# Revit family: 05-60-001-DN50-300.rfatest
name_source: partatom
category: Pipe Accessories
units: mm (PartAtom-declared; Revit-internal decimal feet)

## family parameters
Always vertical = Yes
Cut with Voids When Loaded = No
Part Type = Valve - Breaks Into
Round Connector Dimension = Use Diameter
Shared = No
Work Plane-Based = No

## types (18) — shared parameters
1 = 1 mm  [stored 0.00328084 ft]
10 = 10 mm  [stored 0.0328084 ft]
3 = 3 mm  [stored 0.00984252 ft]
5 = 5 mm  [stored 0.0164042 ft]
DN050_ PN10/16_Dd63 = 05-050-60-1600
DN060_ PN10/16_Dd63 = 05-063-60-1600
DN065_ PN10/16_Dd75 = 05-075-60-1600
DN080_ PN10/16_Dd90 = 05-090-60-1600
DN100_ PN10/16_Dd110 = 05-110-60-1600
DN125_ PN10/16_Dd125 = 05-125-60-1600
DN125_ PN10/16_Dd140 = 05-140-60-1600
DN150_ PN10/16_Dd160 = 05-160-60-1600
DN200_ PN10_Dd200 = 05-200-60-0600
DN200_ PN10_Dd225 = 05-200-60-1600
DN200_ PN16_Dd200 = 05-225-60-0600
DN200_ PN16_Dd225 = 05-225-60-1600
DN250_ PN10_Dd250 = 05-250-60-0600
DN250_ PN10_Dd280 = 05-250-60-1600
DN250_ PN16_Dd250 = 05-280-60-0600
DN250_ PN16_Dd280 = 05-280-60-1600
DN300_ PN10_Dd315 = 05-315-60-0600
DN300_ PN16_Dd315 = 05-315-60-1600
Description_ = AVK COMBI-FLANGE FOR PE AND PVC PIPES, PN10/16
EPDM = 6 mm  [stored 0.019685 ft]
Epdm = 2 mm  [stored 0.00656168 ft]
FL_T1 = 3 mm  [stored 0.00984252 ft]
Search_table = 05-60-001-DN50-300
URL_product_pages = https://www.avkvalves.com
zero-valued in all types: Default Elevation, L4

## per-type parameters (varying)
| type | (D-Dd)1 | Bore | D | DN | Dd | FL_T | Flange_H | L | L-L9 | L/2 | L1 | L2 | L6 | L9 | Thickness | Thickness1 |
| DN100_ PN10/16_Dd110 | 19 mm  [stored 0.062336 ft] | 50 mm  [stored 0.164042 ft] | 110 mm | 100 mm | 55 mm  [stored 0.180446 ft] | 5 mm  [stored 0.0164042 ft] | 8 mm  [stored 0.0262467 ft] | 99 mm | 72 mm | 50 mm  [stored 0.164042 ft] | 35 mm | 149 mm | 20 mm  [stored 0.0656168 ft] | 27 mm  [stored 0.0885827 ft] | 5 mm  [stored 0.0164042 ft] | 10 mm  [stored 0.0328084 ft] |
| DN125_ PN10/16_Dd125 | 22 mm | 63 mm  [stored 0.206693 ft] | 125 mm | 125 mm | 63 mm  [stored 0.206693 ft] | 5 mm  [stored 0.0164042 ft] | 9 mm  [stored 0.0295276 ft] | 101 mm | 74 mm | 51 mm | 35 mm | 152 mm | 20 mm  [stored 0.0656168 ft] | 27 mm  [stored 0.0885827 ft] | 5 mm  [stored 0.0164042 ft] | 10 mm  [stored 0.0328084 ft] |
| DN125_ PN10/16_Dd140 | 19 mm  [stored 0.062336 ft] | 63 mm  [stored 0.206693 ft] | 125 mm | 125 mm | 70 mm | 5 mm  [stored 0.0164042 ft] | 8 mm  [stored 0.0262467 ft] | 103 mm | 76 mm | 52 mm | 35 mm | 155 mm | 21 mm  [stored 0.0688976 ft] | 27 mm  [stored 0.0885827 ft] | 5 mm  [stored 0.0164042 ft] | 10 mm  [stored 0.0328084 ft] |
| DN150_ PN10/16_Dd160 | 22 mm | 75 mm | 143 mm | 150 mm | 80 mm | 5 mm  [stored 0.0164042 ft] | 9 mm  [stored 0.0295276 ft] | 105 mm | 78 mm | 53 mm | 35 mm | 158 mm | 21 mm  [stored 0.0688976 ft] | 27 mm  [stored 0.0885827 ft] | 5 mm  [stored 0.0164042 ft] | 10 mm  [stored 0.0328084 ft] |
| DN200_ PN10_Dd200 | 25 mm  [stored 0.082021 ft] | 100 mm | 170 mm | 200 mm | 100 mm | 8 mm  [stored 0.0262467 ft] | 11 mm | 107 mm | 80 mm | 54 mm | 35 mm | 161 mm | 21 mm  [stored 0.0688976 ft] | 27 mm  [stored 0.0885827 ft] | 6 mm  [stored 0.019685 ft] | 15 mm  [stored 0.0492126 ft] |
| DN200_ PN10_Dd225 | 20 mm  [stored 0.0656168 ft] | 100 mm | 170 mm | 200 mm | 113 mm | 8 mm  [stored 0.0262467 ft] | 9 mm  [stored 0.0295276 ft] | 115 mm | 88 mm | 58 mm | 35 mm | 173 mm | 23 mm  [stored 0.0754593 ft] | 27 mm  [stored 0.0885827 ft] | 6 mm  [stored 0.019685 ft] | 15 mm  [stored 0.0492126 ft] |
| DN200_ PN16_Dd200 | 25 mm  [stored 0.082021 ft] | 100 mm | 170 mm | 200 mm | 100 mm | 8 mm  [stored 0.0262467 ft] | 11 mm | 107 mm | 80 mm | 54 mm | 35 mm | 161 mm | 21 mm  [stored 0.0688976 ft] | 27 mm  [stored 0.0885827 ft] | 6 mm  [stored 0.019685 ft] | 15 mm  [stored 0.0492126 ft] |
| DN200_ PN16_Dd225 | 20 mm  [stored 0.0656168 ft] | 100 mm | 170 mm | 200 mm | 113 mm | 8 mm  [stored 0.0262467 ft] | 9 mm  [stored 0.0295276 ft] | 123 mm | 96 mm | 62 mm | 35 mm | 185 mm | 25 mm  [stored 0.082021 ft] | 27 mm  [stored 0.0885827 ft] | 6 mm  [stored 0.019685 ft] | 15 mm  [stored 0.0492126 ft] |
| DN250_ PN10_Dd250 | 25 mm  [stored 0.082021 ft] | 125 mm | 198 mm | 250 mm | 125 mm | 8 mm  [stored 0.0262467 ft] | 11 mm | 115 mm | 88 mm | 58 mm | 35 mm | 173 mm | 23 mm  [stored 0.0754593 ft] | 27 mm  [stored 0.0885827 ft] | 6 mm  [stored 0.019685 ft] | 15 mm  [stored 0.0492126 ft] |
| DN250_ PN10_Dd280 | 20 mm  [stored 0.0656168 ft] | 125 mm | 198 mm | 250 mm | 140 mm | 8 mm  [stored 0.0262467 ft] | 9 mm  [stored 0.0295276 ft] | 123 mm | 92 mm | 62 mm | 40 mm  [stored 0.131234 ft] | 185 mm | 25 mm  [stored 0.082021 ft] | 31 mm  [stored 0.101706 ft] | 6 mm  [stored 0.019685 ft] | 15 mm  [stored 0.0492126 ft] |
| DN250_ PN16_Dd250 | 25 mm  [stored 0.082021 ft] | 125 mm | 198 mm | 250 mm | 125 mm | 8 mm  [stored 0.0262467 ft] | 11 mm | 123 mm | 96 mm | 62 mm | 35 mm | 185 mm | 25 mm  [stored 0.082021 ft] | 27 mm  [stored 0.0885827 ft] | 6 mm  [stored 0.019685 ft] | 15 mm  [stored 0.0492126 ft] |
| DN250_ PN16_Dd280 | 20 mm  [stored 0.0656168 ft] | 125 mm | 198 mm | 250 mm | 140 mm | 8 mm  [stored 0.0262467 ft] | 9 mm  [stored 0.0295276 ft] | 131 mm | 100 mm | 66 mm | 40 mm  [stored 0.131234 ft] | 197 mm | 26 mm | 31 mm  [stored 0.101706 ft] | 6 mm  [stored 0.019685 ft] | 15 mm  [stored 0.0492126 ft] |
| DN300_ PN10_Dd315 | 23 mm  [stored 0.0754593 ft] | 150 mm | 223 mm | 300 mm | 158 mm | 8 mm  [stored 0.0262467 ft] | 10 mm  [stored 0.0328084 ft] | 125 mm | 94 mm | 63 mm  [stored 0.206693 ft] | 40 mm  [stored 0.131234 ft] | 188 mm | 25 mm  [stored 0.082021 ft] | 31 mm  [stored 0.101706 ft] | 6 mm  [stored 0.019685 ft] | 15 mm  [stored 0.0492126 ft] |
| DN300_ PN16_Dd315 | 23 mm  [stored 0.0754593 ft] | 150 mm | 223 mm | 300 mm | 158 mm | 5 mm  [stored 0.0164042 ft] | 10 mm  [stored 0.0328084 ft] | 133 mm | 102 mm | 67 mm | 40 mm  [stored 0.131234 ft] | 200 mm | 27 mm  [stored 0.0885827 ft] | 31 mm  [stored 0.101706 ft] | 6 mm  [stored 0.019685 ft] | 10 mm  [stored 0.0328084 ft] |
| DN050_ PN10/16_Dd63 | 18 mm  [stored 0.0590551 ft] | 25 mm  [stored 0.082021 ft] | 83 mm | 50 mm  [stored 0.164042 ft] | 32 mm | 5 mm  [stored 0.0164042 ft] | 8 mm  [stored 0.0262467 ft] | 97 mm | 70 mm | 49 mm  [stored 0.160761 ft] | 35 mm | 146 mm | 19 mm  [stored 0.062336 ft] | 27 mm  [stored 0.0885827 ft] | 5 mm  [stored 0.0164042 ft] | 10 mm  [stored 0.0328084 ft] |
| DN060_ PN10/16_Dd63 | 20 mm  [stored 0.0656168 ft] | 30 mm  [stored 0.0984252 ft] | 88 mm | 60 mm  [stored 0.19685 ft] | 32 mm | 5 mm  [stored 0.0164042 ft] | 8 mm  [stored 0.0262467 ft] | 97 mm | 70 mm | 49 mm  [stored 0.160761 ft] | 35 mm | 146 mm | 19 mm  [stored 0.062336 ft] | 27 mm  [stored 0.0885827 ft] | 5 mm  [stored 0.0164042 ft] | 10 mm  [stored 0.0328084 ft] |
| DN065_ PN10/16_Dd75 | 19 mm  [stored 0.062336 ft] | 33 mm | 93 mm | 65 mm  [stored 0.213255 ft] | 38 mm | 5 mm  [stored 0.0164042 ft] | 8 mm  [stored 0.0262467 ft] | 97 mm | 70 mm | 49 mm  [stored 0.160761 ft] | 35 mm | 146 mm | 19 mm  [stored 0.062336 ft] | 27 mm  [stored 0.0885827 ft] | 5 mm  [stored 0.0164042 ft] | 10 mm  [stored 0.0328084 ft] |
| DN080_ PN10/16_Dd90 | 19 mm  [stored 0.062336 ft] | 40 mm  [stored 0.131234 ft] | 100 mm | 80 mm | 45 mm  [stored 0.147638 ft] | 5 mm  [stored 0.0164042 ft] | 8 mm  [stored 0.0262467 ft] | 98 mm | 71 mm | 49 mm  [stored 0.160761 ft] | 35 mm | 147 mm | 20 mm  [stored 0.0656168 ft] | 27 mm  [stored 0.0885827 ft] | 5 mm  [stored 0.0164042 ft] | 10 mm  [stored 0.0328084 ft] |

note: [stored X ft] marks values corroborated as IEEE doubles in the binary element streams (Revit-internal decimal feet)

## geometry (parser evidence)
native form markers: Sweep x15
no freeform markers — native parametric forms only
